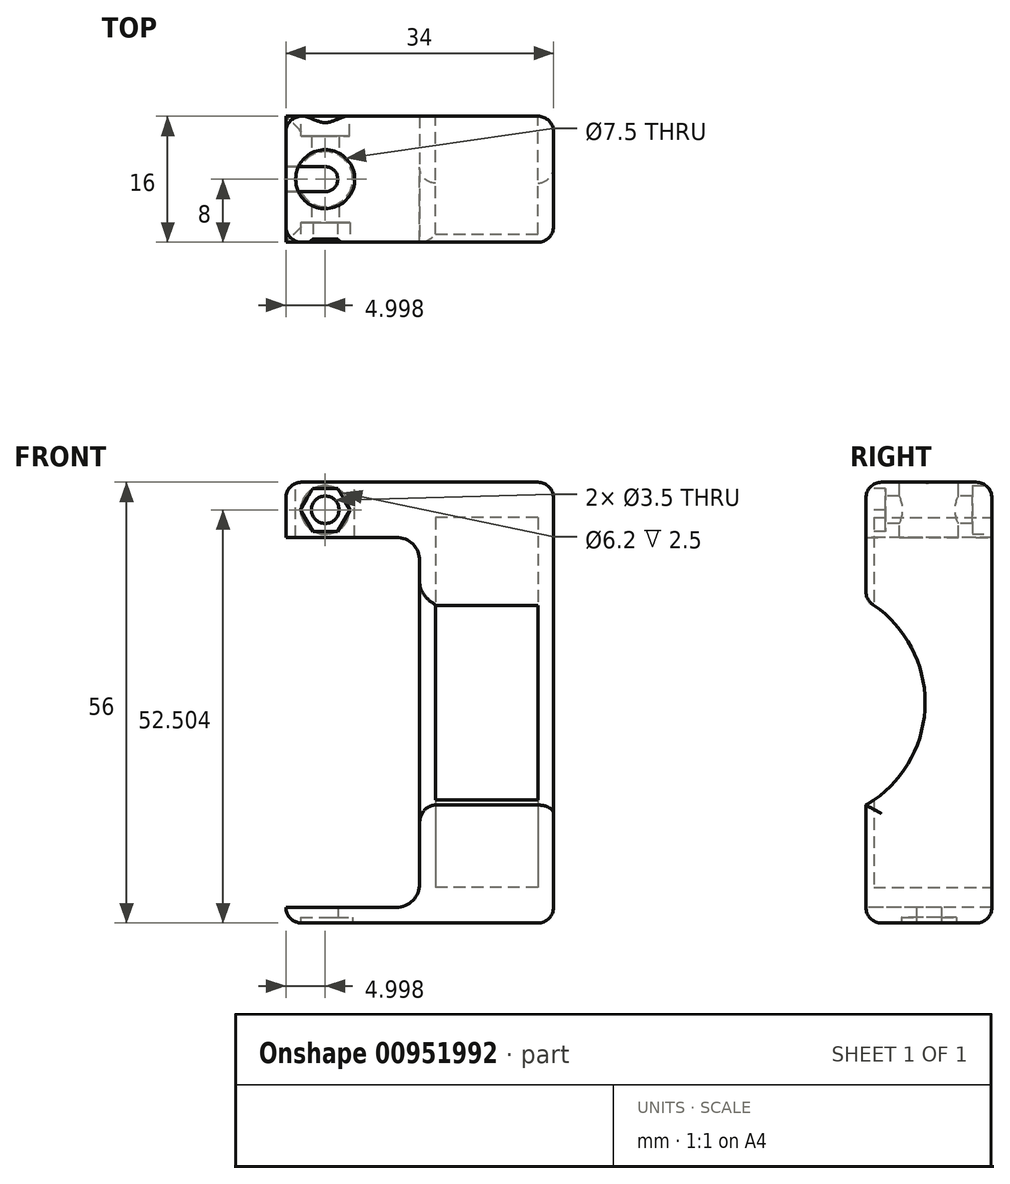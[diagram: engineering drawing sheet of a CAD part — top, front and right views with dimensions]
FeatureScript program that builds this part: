
annotation { "Feature Type Name" : "Feature", "Feature Type Description" : "" }
export const myFeature = defineFeature(function(context is Context, id is Id, definition is map)
    precondition{}
    {
        {
            var Q0;
            Q0=qCreatedBy(makeId("Front.planeOp"),FACE);
            var sketch = newSketch(context, id + "F0", { "sketchPlane" : qUnion([Q0])});
            skLineSegment(sketch, "E0.bottom", {"start": v(-10.31, 31.17) * mm, "end": v(23.69, 31.17) * mm});
            skLineSegment(sketch, "E0.top", {"start": v(-10.31, -24.83) * mm, "end": v(23.69, -24.83) * mm});
            skLineSegment(sketch, "E0.left", {"start": v(-10.31, 31.17) * mm, "end": v(-10.31, -24.83) * mm});
            skLineSegment(sketch, "E0.right", {"start": v(23.69, 31.17) * mm, "end": v(23.69, -24.83) * mm});
            skSolve(sketch);
        }
        {
            var Q0;
            Q0=makeQuery(id+"F0.imprint","IMPRINT",FACE,{"disambiguationData":[TD([[makeQuery(id+"F0.imprint","IMPRINT",EDGE,{"derivedFrom":sQuery(id+"F0.wireOp",EDGE,"E0.bottom")}),-1.0]])]});
            extrude(context, id + "F1", {"entities" : qUnion([Q0]), "depth" : 8 * mm, "offsetDistance" : 25 * mm, "hasSecondDirection" : true, "secondDirectionOppositeDirection" : true, "secondDirectionDepth" : 8 * mm});
        }
        {
            var Q0;
            Q0=makeQuery(id+"F1.opExtrude","CAP_FACE",FACE,{"disambiguationData":[OSD([sQuery(id+"F0.wireOp",EDGE,"E0.bottom"),sQuery(id+"F0.wireOp",EDGE,"E0.top"),sQuery(id+"F0.wireOp",EDGE,"E0.left"),sQuery(id+"F0.wireOp",EDGE,"E0.right")])],"isStart":false});
            var sketch = newSketch(context, id + "F2", { "sketchPlane" : qUnion([Q0])});
            skLineSegment(sketch, "E1.bottom", {"start": v(-10.31, -22.83) * mm, "end": v(3.69, -22.83) * mm});
            skLineSegment(sketch, "E1.top", {"start": v(-10.31, 24.17) * mm, "end": v(3.69, 24.17) * mm});
            skLineSegment(sketch, "E1.left", {"start": v(-10.31, -22.83) * mm, "end": v(-10.31, 24.17) * mm});
            skLineSegment(sketch, "E1.right", {"start": v(6.69, -19.83) * mm, "end": v(6.69, 21.17) * mm});
            skCircle(sketch, "E2", {"center": v(-5.31, 27.67) * mm, "radius": 1.75 * mm});
            skLineSegment(sketch, "E3.top", {"start": v(6.69, 21.17) * mm, "end": v(3.69, 21.17) * mm, "construction": true});
            skLineSegment(sketch, "E3.right", {"start": v(3.69, 24.17) * mm, "end": v(3.69, 21.17) * mm, "construction": true});
            skArc(sketch, "E4", {"start": v(6.69, 21.17) * mm, "mid": v(5.8, 23.3) * mm, "end": v(3.69, 24.17) * mm});
            skLineSegment(sketch, "E5.top", {"start": v(6.69, -19.83) * mm, "end": v(3.69, -19.83) * mm, "construction": true});
            skLineSegment(sketch, "E5.right", {"start": v(3.69, -22.83) * mm, "end": v(3.69, -19.83) * mm, "construction": true});
            skArc(sketch, "E6", {"start": v(3.69, -22.83) * mm, "mid": v(5.8, -21.95) * mm, "end": v(6.69, -19.83) * mm});
            skSolve(sketch);
        }
        {
            var Q0;
            Q0 = qSketchRegion(id + "F2", true);
            extrude(context, id + "F3", {"entities" : qUnion([Q0]), "operationType" : NewBodyOperationType.REMOVE, "oppositeDirection" : true, "depth" : 25 * mm, "offsetDistance" : 25 * mm});
        }
        {
            var Q0;
            Q0=makeQuery(id+"F1.opExtrude","SWEPT_FACE",FACE,{"disambiguationData":[OSD([sQuery(id+"F0.wireOp",EDGE,"E0.bottom")])]});
            var sketch = newSketch(context, id + "F4", { "sketchPlane" : qUnion([Q0])});
            skCircle(sketch, "E7", {"center": v(-5.31, 0) * mm, "radius": 3.75 * mm});
            skSolve(sketch);
        }
        {
            var Q0;
            Q0=makeQuery(id+"F4.imprint","IMPRINT",FACE,{"disambiguationData":[TD([[makeQuery(id+"F4.imprint","IMPRINT",EDGE,{"derivedFrom":sQuery(id+"F4.wireOp",EDGE,"E7")}),1.0]])]});
            extrude(context, id + "F5", {"entities" : qUnion([Q0]), "operationType" : NewBodyOperationType.REMOVE, "oppositeDirection" : true, "depth" : 25 * mm, "offsetDistance" : 25 * mm});
        }
        {
            var Q0;
            Q0=makeQuery(id+"F1.opExtrude","CAP_FACE",FACE,{"disambiguationData":[OSD([sQuery(id+"F0.wireOp",EDGE,"E0.bottom"),sQuery(id+"F0.wireOp",EDGE,"E0.top"),sQuery(id+"F0.wireOp",EDGE,"E0.left"),sQuery(id+"F0.wireOp",EDGE,"E0.right")])],"isStart":false});
            var sketch = newSketch(context, id + "F6", { "sketchPlane" : qUnion([Q0])});
            skPoint(sketch, "E8.center.orphan", {"position": v(-5.31, 27.67) * mm});
            skCircle(sketch, "E9", {"center": v(-5.31, 27.67) * mm, "radius": 3.15 * mm, "construction": true});
            skLineSegment(sketch, "E10.0", {"start": v(-6.89, 30.4) * mm, "end": v(-3.74, 30.4) * mm});
            skLineSegment(sketch, "E10.1", {"start": v(-3.74, 30.4) * mm, "end": v(-2.16, 27.68) * mm});
            skLineSegment(sketch, "E10.2", {"start": v(-2.16, 27.68) * mm, "end": v(-3.74, 24.95) * mm});
            skLineSegment(sketch, "E10.3", {"start": v(-3.74, 24.95) * mm, "end": v(-6.89, 24.95) * mm});
            skLineSegment(sketch, "E10.4", {"start": v(-6.89, 24.95) * mm, "end": v(-8.46, 27.67) * mm});
            skLineSegment(sketch, "E10.5", {"start": v(-8.46, 27.67) * mm, "end": v(-6.89, 30.4) * mm});
            skSolve(sketch);
        }
        {
            var Q0;
            Q0=makeQuery(id+"F6.imprint","IMPRINT",FACE,{"disambiguationData":[TD([[makeQuery(id+"F6.imprint","IMPRINT",EDGE,{"derivedFrom":sQuery(id+"F6.wireOp",EDGE,"E8")}),1.0]])]});
            var Q1;
            Q1=makeQuery(id+"F6.imprint","IMPRINT",FACE,{"disambiguationData":[TD([[makeQuery(id+"F6.imprint","IMPRINT",EDGE,{"derivedFrom":sQuery(id+"F6.wireOp",EDGE,"E10.0")}),-1.0]])]});
            extrude(context, id + "F7", {"entities" : qUnion([Q0, Q1]), "operationType" : NewBodyOperationType.REMOVE, "oppositeDirection" : true, "depth" : 2.5 * mm, "offsetDistance" : 25 * mm});
        }
        {
            var Q0;
            Q0=makeQuery(id+"F1.opExtrude","CAP_FACE",FACE,{"disambiguationData":[OSD([sQuery(id+"F0.wireOp",EDGE,"E0.bottom"),sQuery(id+"F0.wireOp",EDGE,"E0.top"),sQuery(id+"F0.wireOp",EDGE,"E0.left"),sQuery(id+"F0.wireOp",EDGE,"E0.right")])],"isStart":true});
            var sketch = newSketch(context, id + "F8", { "sketchPlane" : qUnion([Q0])});
            skCircle(sketch, "E11", {"center": v(5.31, 27.67) * mm, "radius": 3.1 * mm});
            skSolve(sketch);
        }
        {
            var Q0;
            Q0=makeQuery(id+"F8.imprint","IMPRINT",FACE,{"disambiguationData":[TD([[makeQuery(id+"F8.imprint","IMPRINT",EDGE,{"derivedFrom":sQuery(id+"F8.wireOp",EDGE,"E11")}),1.0]])]});
            extrude(context, id + "F9", {"entities" : qUnion([Q0]), "operationType" : NewBodyOperationType.REMOVE, "oppositeDirection" : true, "depth" : 2.5 * mm, "offsetDistance" : 25 * mm});
        }
        {
            var Q0;
            Q0=makeQuery(id+"F1.opExtrude","SWEPT_FACE",FACE,{"disambiguationData":[OSD([sQuery(id+"F0.wireOp",EDGE,"E0.top")])]});
            var sketch = newSketch(context, id + "F10", { "sketchPlane" : qUnion([Q0])});
            skArc(sketch, "E12", {"start": v(-5.31, -1.6) * mm, "mid": v(-3.71, 0) * mm, "end": v(-5.31, 1.6) * mm});
            skLineSegment(sketch, "E13.bottom", {"start": v(-5.31, -1.6) * mm, "end": v(-10.31, -1.6) * mm});
            skLineSegment(sketch, "E13.top", {"start": v(-5.31, 1.6) * mm, "end": v(-10.31, 1.6) * mm});
            skLineSegment(sketch, "E13.right", {"start": v(-10.31, -1.6) * mm, "end": v(-10.31, 1.6) * mm});
            skSolve(sketch);
        }
        {
            var Q0;
            Q0=makeQuery(id+"F10.imprint","IMPRINT",FACE,{"disambiguationData":[TD([[makeQuery(id+"F10.imprint","IMPRINT",EDGE,{"derivedFrom":sQuery(id+"F10.wireOp",EDGE,"E12")}),1.0]])]});
            extrude(context, id + "F11", {"entities" : qUnion([Q0]), "operationType" : NewBodyOperationType.REMOVE, "oppositeDirection" : true, "depth" : 10 * mm, "offsetDistance" : 25 * mm});
        }
        {
            var Q0;
            Q0=makeQuery(id+"F1.opExtrude","SWEPT_FACE",FACE,{"disambiguationData":[OSD([sQuery(id+"F0.wireOp",EDGE,"E0.top")])]});
            var sketch = newSketch(context, id + "F12", { "sketchPlane" : qUnion([Q0])});
            skCircle(sketch, "E14", {"center": v(-5.31, 0) * mm, "radius": 3.5 * mm});
            skSolve(sketch);
        }
        {
            var Q0;
            Q0=makeQuery(id+"F12.imprint","IMPRINT",FACE,{"disambiguationData":[TD([[makeQuery(id+"F12.imprint","IMPRINT",EDGE,{"derivedFrom":sQuery(id+"F12.wireOp",EDGE,"E14")}),1.0]])]});
            extrude(context, id + "F13", {"entities" : qUnion([Q0]), "operationType" : NewBodyOperationType.REMOVE, "oppositeDirection" : true, "depth" : 0.75 * mm, "offsetDistance" : 25 * mm});
        }
        {
            var Q0;
            Q0=makeQuery(id+"F1.opExtrude","CAP_FACE",FACE,{"disambiguationData":[OSD([sQuery(id+"F0.wireOp",EDGE,"E0.bottom"),sQuery(id+"F0.wireOp",EDGE,"E0.top"),sQuery(id+"F0.wireOp",EDGE,"E0.left"),sQuery(id+"F0.wireOp",EDGE,"E0.right")])],"isStart":true});
            var sketch = newSketch(context, id + "F14", { "sketchPlane" : qUnion([Q0])});
            skLineSegment(sketch, "E15.bottom", {"start": v(-21.69, 26.67) * mm, "end": v(-8.69, 26.67) * mm});
            skLineSegment(sketch, "E15.top", {"start": v(-21.69, -20.33) * mm, "end": v(-8.69, -20.33) * mm});
            skLineSegment(sketch, "E15.left", {"start": v(-21.69, 26.67) * mm, "end": v(-21.69, -20.33) * mm});
            skLineSegment(sketch, "E15.right", {"start": v(-8.69, 26.67) * mm, "end": v(-8.69, -20.33) * mm});
            skSolve(sketch);
        }
        {
            var Q0;
            Q0=makeQuery(id+"F14.imprint","IMPRINT",FACE,{"disambiguationData":[TD([[makeQuery(id+"F14.imprint","IMPRINT",EDGE,{"derivedFrom":sQuery(id+"F14.wireOp",EDGE,"E15.bottom")}),-1.0]])]});
            extrude(context, id + "F15", {"entities" : qUnion([Q0]), "operationType" : NewBodyOperationType.REMOVE, "oppositeDirection" : true, "depth" : 15 * mm, "offsetDistance" : 25 * mm});
        }
        {
            var Q0;
            Q0=makeQuery(id+"F1.opExtrude","SWEPT_FACE",FACE,{"disambiguationData":[OSD([sQuery(id+"F0.wireOp",EDGE,"E0.right")])]});
            var sketch = newSketch(context, id + "F16", { "sketchPlane" : qUnion([Q0])});
            skLineSegment(sketch, "E16", {"start": v(-15.36, 16.17) * mm, "end": v(16.16, 16.17) * mm, "construction": true});
            skLineSegment(sketch, "E17", {"start": v(-15.36, -9.83) * mm, "end": v(16.16, -9.83) * mm, "construction": true});
            skArc(sketch, "E18", {"start": v(-8, -9.83) * mm, "mid": v(-0.48, 3.17) * mm, "end": v(-8, 16.17) * mm});
            skSolve(sketch);
        }
        {
            var Q0;
            {var subQ0=sQuery(id+"F16.wireOp",EDGE,"E18");Q0=makeQuery(id+"F16.imprint","IMPRINT",FACE,{"disambiguationData":[TD([[makeQuery(id+"F16.imprint","IMPRINT",EDGE,{"derivedFrom":subQ0}),1.0]])]});}
            extrude(context, id + "F17", {"entities" : qUnion([Q0]), "operationType" : NewBodyOperationType.REMOVE, "oppositeDirection" : true, "depth" : 25 * mm, "offsetDistance" : 25 * mm});
        }
        {
            var Q0;
            Q0=makeQuery(id+"F1.opExtrude","CAP_EDGE",EDGE,{"disambiguationData":[OSD([sQuery(id+"F0.wireOp",EDGE,"E0.bottom")])],"isStart":true});
            var Q1;
            Q1=makeQuery(id+"F1.opExtrude","SWEPT_EDGE",EDGE,{"disambiguationData":[OSD([sQuery(id+"F0.wireOp",EDGE,"E0.bottom"),sQuery(id+"F0.wireOp",EDGE,"E0.left")])]});
            var Q2;
            {var subQ0=sQuery(id+"F0.wireOp",EDGE,"E0.bottom");var subQ1=sQuery(id+"F0.wireOp",EDGE,"E0.left");Q2=makeQuery(id+"F3.boolean.opBoolean","SPLIT",EDGE,{"disambiguationData":[TD([makeQuery(id+"F1.opExtrude","SWEPT_FACE",FACE,{"disambiguationData":[OSD([subQ0])]})])],"derivedFrom":makeQuery(id+"F1.opExtrude","CAP_EDGE",EDGE,{"disambiguationData":[OSD([subQ1])],"isStart":true})});}
            var Q3;
            {var subQ0=sQuery(id+"F0.wireOp",EDGE,"E0.bottom");var subQ1=sQuery(id+"F0.wireOp",EDGE,"E0.left");Q3=makeQuery(id+"F3.boolean.opBoolean","SPLIT",EDGE,{"disambiguationData":[TD([makeQuery(id+"F1.opExtrude","SWEPT_FACE",FACE,{"disambiguationData":[OSD([subQ0])]})])],"derivedFrom":makeQuery(id+"F1.opExtrude","CAP_EDGE",EDGE,{"disambiguationData":[OSD([subQ1])],"isStart":false})});}
            var Q4;
            Q4=makeQuery(id+"F1.opExtrude","CAP_EDGE",EDGE,{"disambiguationData":[OSD([sQuery(id+"F0.wireOp",EDGE,"E0.bottom")])],"isStart":false});
            var Q5;
            Q5=makeQuery(id+"F1.opExtrude","CAP_EDGE",EDGE,{"disambiguationData":[OSD([sQuery(id+"F0.wireOp",EDGE,"E0.right")])],"isStart":true});
            var Q6;
            {var subQ0=sQuery(id+"F0.wireOp",EDGE,"E0.bottom");var subQ1=sQuery(id+"F0.wireOp",EDGE,"E0.right");Q6=makeQuery(id+"F17.boolean.opBoolean","SPLIT",EDGE,{"disambiguationData":[TD([makeQuery(id+"F1.opExtrude","SWEPT_FACE",FACE,{"disambiguationData":[OSD([subQ0])]})])],"derivedFrom":makeQuery(id+"F1.opExtrude","CAP_EDGE",EDGE,{"disambiguationData":[OSD([subQ1])],"isStart":false})});}
            var Q7;
            Q7=makeQuery(id+"F1.opExtrude","SWEPT_FACE",FACE,{"disambiguationData":[OSD([sQuery(id+"F0.wireOp",EDGE,"E0.right")])]});
            var Q8;
            {var subQ0=sQuery(id+"F16.wireOp",EDGE,"E18");var subQ1=sQuery(id+"F0.wireOp",EDGE,"E0.right");Q8=makeQuery(id+"F17.boolean.opBoolean","COPY",EDGE,{"derivedFrom":makeQuery(id+"F17.opExtrude","SWEPT_EDGE",EDGE,{"disambiguationData":[OSD([subQ1,subQ0]),TDD([makeQuery(id+"F16.imprint","INTERSECT",VERTEX,{"disambiguationData":[OD(0.0)],"derivedFrom":[makeQuery(id+"F1.opExtrude","CAP_EDGE",EDGE,{"disambiguationData":[OSD([subQ1])],"isStart":false}),subQ0]})])]})});}
            var Q9;
            {var subQ0=sQuery(id+"F16.wireOp",EDGE,"E18");var subQ1=sQuery(id+"F0.wireOp",EDGE,"E0.right");Q9=makeQuery(id+"F17.boolean.opBoolean","COPY",EDGE,{"derivedFrom":makeQuery(id+"F17.opExtrude","SWEPT_EDGE",EDGE,{"disambiguationData":[OSD([subQ1,subQ0]),TDD([makeQuery(id+"F16.imprint","INTERSECT",VERTEX,{"disambiguationData":[OD(1.0)],"derivedFrom":[makeQuery(id+"F1.opExtrude","CAP_EDGE",EDGE,{"disambiguationData":[OSD([subQ1])],"isStart":false}),subQ0]})])]})});}
            var Q10;
            Q10=makeQuery(id+"F17.boolean.opBoolean","INTERSECT",EDGE,{"derivedFrom":[makeQuery(id+"F3.boolean.opBoolean","COPY",FACE,{"derivedFrom":makeQuery(id+"F3.opExtrude","SWEPT_FACE",FACE,{"disambiguationData":[OSD([sQuery(id+"F2.wireOp",EDGE,"E1.right")])]})}),makeQuery(id+"F17.opExtrude","SWEPT_FACE",FACE,{"disambiguationData":[OSD([sQuery(id+"F16.wireOp",EDGE,"E18")])]})]});
            var Q11;
            Q11=makeQuery(id+"F15.boolean.opBoolean","COPY",EDGE,{"derivedFrom":makeQuery(id+"F15.opExtrude","CAP_EDGE",EDGE,{"disambiguationData":[OSD([sQuery(id+"F14.wireOp",EDGE,"E15.right")])],"isStart":true})});
            var Q12;
            Q12=makeQuery(id+"F15.boolean.opBoolean","COPY",EDGE,{"derivedFrom":makeQuery(id+"F15.opExtrude","CAP_EDGE",EDGE,{"disambiguationData":[OSD([sQuery(id+"F14.wireOp",EDGE,"E15.bottom")])],"isStart":true})});
            var Q13;
            Q13=makeQuery(id+"F15.boolean.opBoolean","COPY",EDGE,{"derivedFrom":makeQuery(id+"F15.opExtrude","CAP_EDGE",EDGE,{"disambiguationData":[OSD([sQuery(id+"F14.wireOp",EDGE,"E15.left")])],"isStart":true})});
            var Q14;
            Q14=makeQuery(id+"F15.boolean.opBoolean","COPY",EDGE,{"derivedFrom":makeQuery(id+"F15.opExtrude","CAP_EDGE",EDGE,{"disambiguationData":[OSD([sQuery(id+"F14.wireOp",EDGE,"E15.top")])],"isStart":true})});
            var Q15;
            Q15=makeQuery(id+"F1.opExtrude","CAP_EDGE",EDGE,{"disambiguationData":[OSD([sQuery(id+"F0.wireOp",EDGE,"E0.top")])],"isStart":true});
            var Q16;
            Q16=makeQuery(id+"F1.opExtrude","CAP_EDGE",EDGE,{"disambiguationData":[OSD([sQuery(id+"F0.wireOp",EDGE,"E0.top")])],"isStart":false});
            var Q17;
            Q17=makeQuery(id+"F1.opExtrude","SWEPT_EDGE",EDGE,{"disambiguationData":[OSD([sQuery(id+"F0.wireOp",EDGE,"E0.top"),sQuery(id+"F0.wireOp",EDGE,"E0.left")])]});
            fillet(context, id + "F18", {"entities" : qUnion([Q0, Q1, Q2, Q3, Q4, Q5, Q6, Q7, Q8, Q9, Q10, Q11, Q12, Q13, Q14, Q15, Q16, Q17]), "radius" : 2 * mm, "tangentPropagation" : true, "allowEdgeOverflow" : false});
        }
    });
